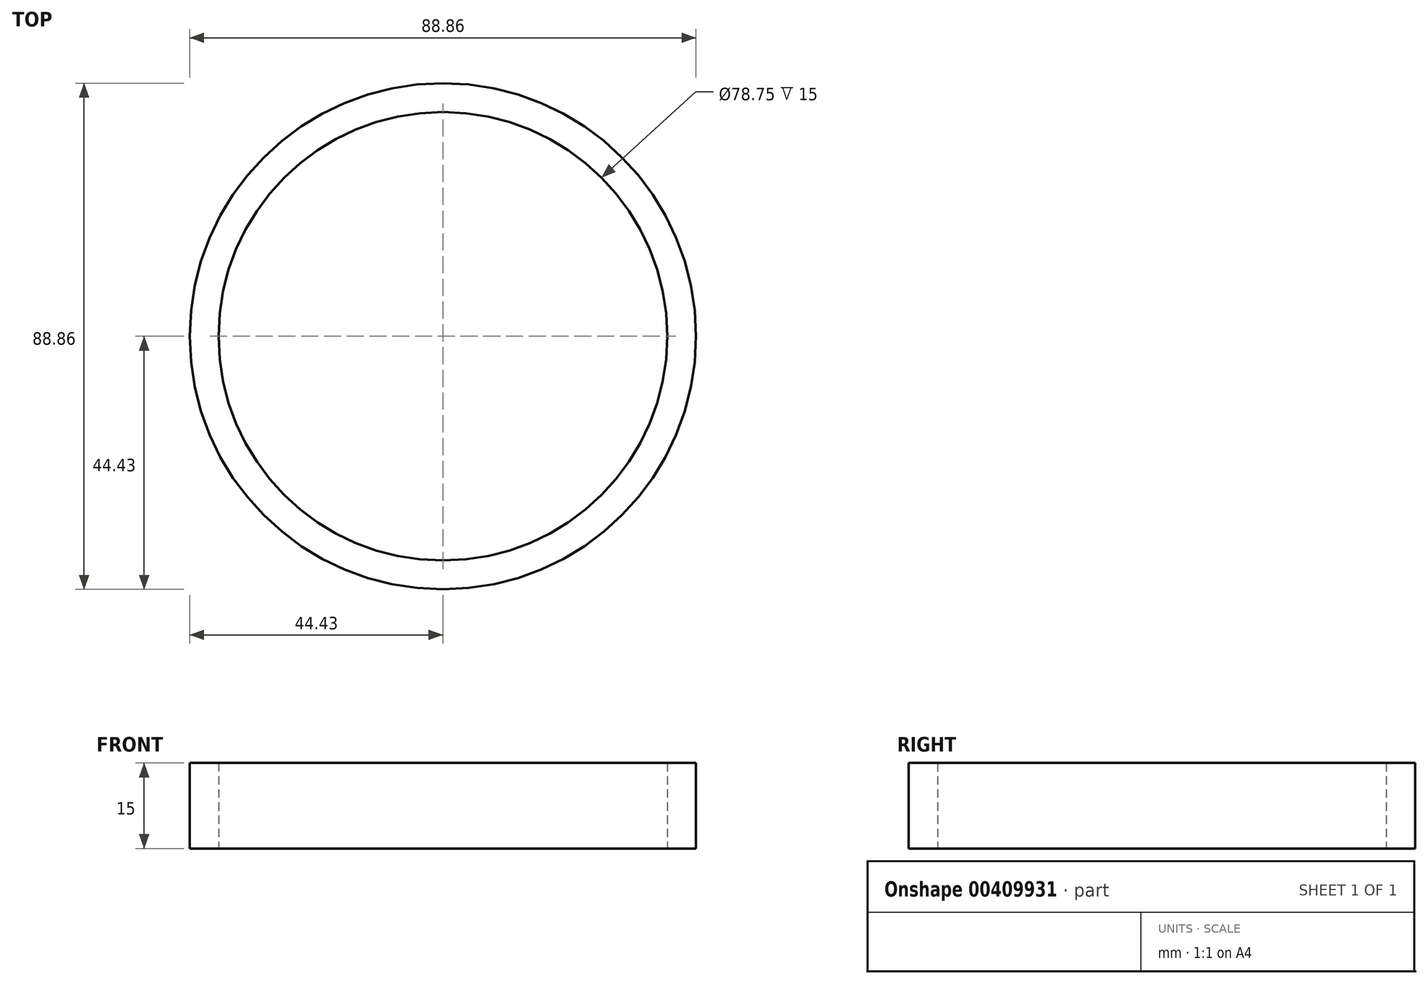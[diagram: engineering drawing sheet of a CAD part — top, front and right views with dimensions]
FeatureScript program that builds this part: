
annotation { "Feature Type Name" : "Feature", "Feature Type Description" : "" }
export const myFeature = defineFeature(function(context is Context, id is Id, definition is map)
    precondition{}
    {
        {
            var Q0;
            Q0=qCreatedBy(makeId("Top.planeOp"),FACE);
            var sketch = newSketch(context, id + "F0", { "sketchPlane" : qUnion([Q0])});
            skCircle(sketch, "E0", {"center": v(0, 0) * mm, "radius": 44.43 * mm});
            skCircle(sketch, "E1", {"center": v(0, 0) * mm, "radius": 39.37 * mm});
            skSolve(sketch);
        }
        {
            var Q0;
            Q0=makeQuery(id+"F0.imprint","IMPRINT",FACE,{"disambiguationData":[TD([[makeQuery(id+"F0.imprint","IMPRINT",EDGE,{"derivedFrom":sQuery(id+"F0.wireOp",EDGE,"E0")}),1.0]])]});
            extrude(context, id + "F1", {"entities" : qUnion([Q0]), "depth" : 15 * mm});
        }
    });
